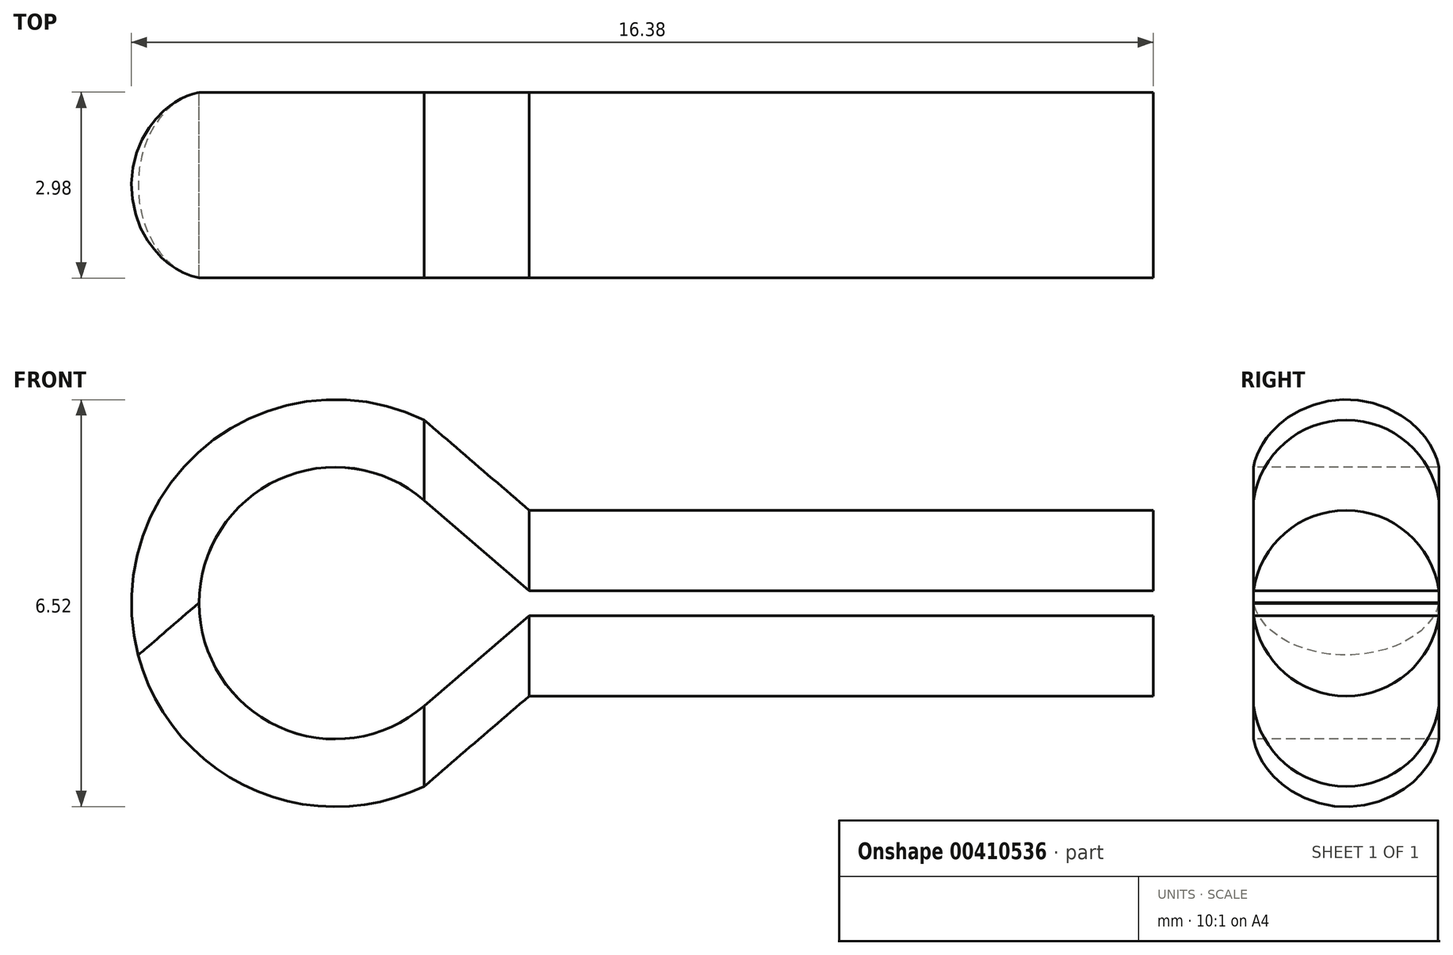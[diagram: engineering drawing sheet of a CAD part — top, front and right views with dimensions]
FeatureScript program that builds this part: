
annotation { "Feature Type Name" : "Feature", "Feature Type Description" : "" }
export const myFeature = defineFeature(function(context is Context, id is Id, definition is map)
    precondition{}
    {
        {
            var Q0;
            Q0=qCreatedBy(makeId("Right.planeOp"),FACE);
            var sketch = newSketch(context, id + "F0", { "sketchPlane" : qUnion([Q0])});
            skCircle(sketch, "E0", {"center": v(0, 0) * mm, "radius": 1.5 * mm, "construction": true});
            skLineSegment(sketch, "E1.bottom", {"start": v(-1.94, 0.2) * mm, "end": v(1.94, 0.2) * mm, "construction": true});
            skLineSegment(sketch, "E1.top", {"start": v(-1.94, -0.2) * mm, "end": v(1.94, -0.2) * mm, "construction": true});
            skLineSegment(sketch, "E1.left", {"start": v(-1.94, 0.2) * mm, "end": v(-1.94, -0.2) * mm, "construction": true});
            skLineSegment(sketch, "E1.right", {"start": v(1.94, 0.2) * mm, "end": v(1.94, -0.2) * mm, "construction": true});
            skArc(sketch, "E2", {"start": v(1.49, 0.2) * mm, "mid": v(0, 1.49) * mm, "end": v(-1.49, 0.2) * mm});
            skLineSegment(sketch, "E3", {"start": v(-1.49, 0.2) * mm, "end": v(1.49, 0.2) * mm});
            skSolve(sketch);
        }
        {
            var Q0;
            Q0=makeQuery(id+"F0.imprint","IMPRINT",FACE,{"disambiguationData":[TD([[makeQuery(id+"F0.imprint","IMPRINT",EDGE,{"derivedFrom":sQuery(id+"F0.wireOp",EDGE,"E2")}),1.0]])]});
            extrude(context, id + "F1", {"entities" : qUnion([Q0]), "oppositeDirection" : true, "depth" : 10 * mm});
        }
        {
            var Q0;
            Q0=qCreatedBy(makeId("Front.planeOp"),FACE);
            var sketch = newSketch(context, id + "F2", { "sketchPlane" : qUnion([Q0])});
            skLineSegment(sketch, "E4", {"start": v(-10, 0) * mm, "end": v(-10, 0.21) * mm});
            skLineSegment(sketch, "E5", {"start": v(-10, 0.21) * mm, "end": v(-11.69, 1.66) * mm});
            skArc(sketch, "E6", {"start": v(-11.69, 1.66) * mm, "mid": v(-14.02, 1.99) * mm, "end": v(-15.3, 0) * mm});
            skSolve(sketch);
        }
        {
            var Q0;
            Q0=makeQuery(id+"F1.opExtrude","CAP_FACE",FACE,{"disambiguationData":[OSD([sQuery(id+"F0.wireOp",EDGE,"E2"),sQuery(id+"F0.wireOp",EDGE,"E3")])],"isStart":false});
            var Q1;
            Q1=sQuery(id+"F2.wireOp",EDGE,"E5");
            var Q2;
            Q2=sQuery(id+"F2.wireOp",EDGE,"E6");
            sweep(context, id + "F3", {"operationType" : NewBodyOperationType.ADD, "profiles" : qUnion([Q0]), "path" : qUnion([Q1, Q2])});
        }
        {
            var Q0;
            Q0=makeQuery(id+"F1.opExtrude","SWEPT_BODY",BODY,{"disambiguationData":[OSD([sQuery(id+"F0.wireOp",EDGE,"E2"),sQuery(id+"F0.wireOp",EDGE,"E3")])]});
            var Q1;
            Q1=qCreatedBy(makeId("Top.planeOp"),FACE);
            mirror(context, id + "F4", {"operationType" : NewBodyOperationType.ADD, "entities" : qUnion([Q0]), "mirrorPlane" : qUnion([Q1])});
        }
    });
